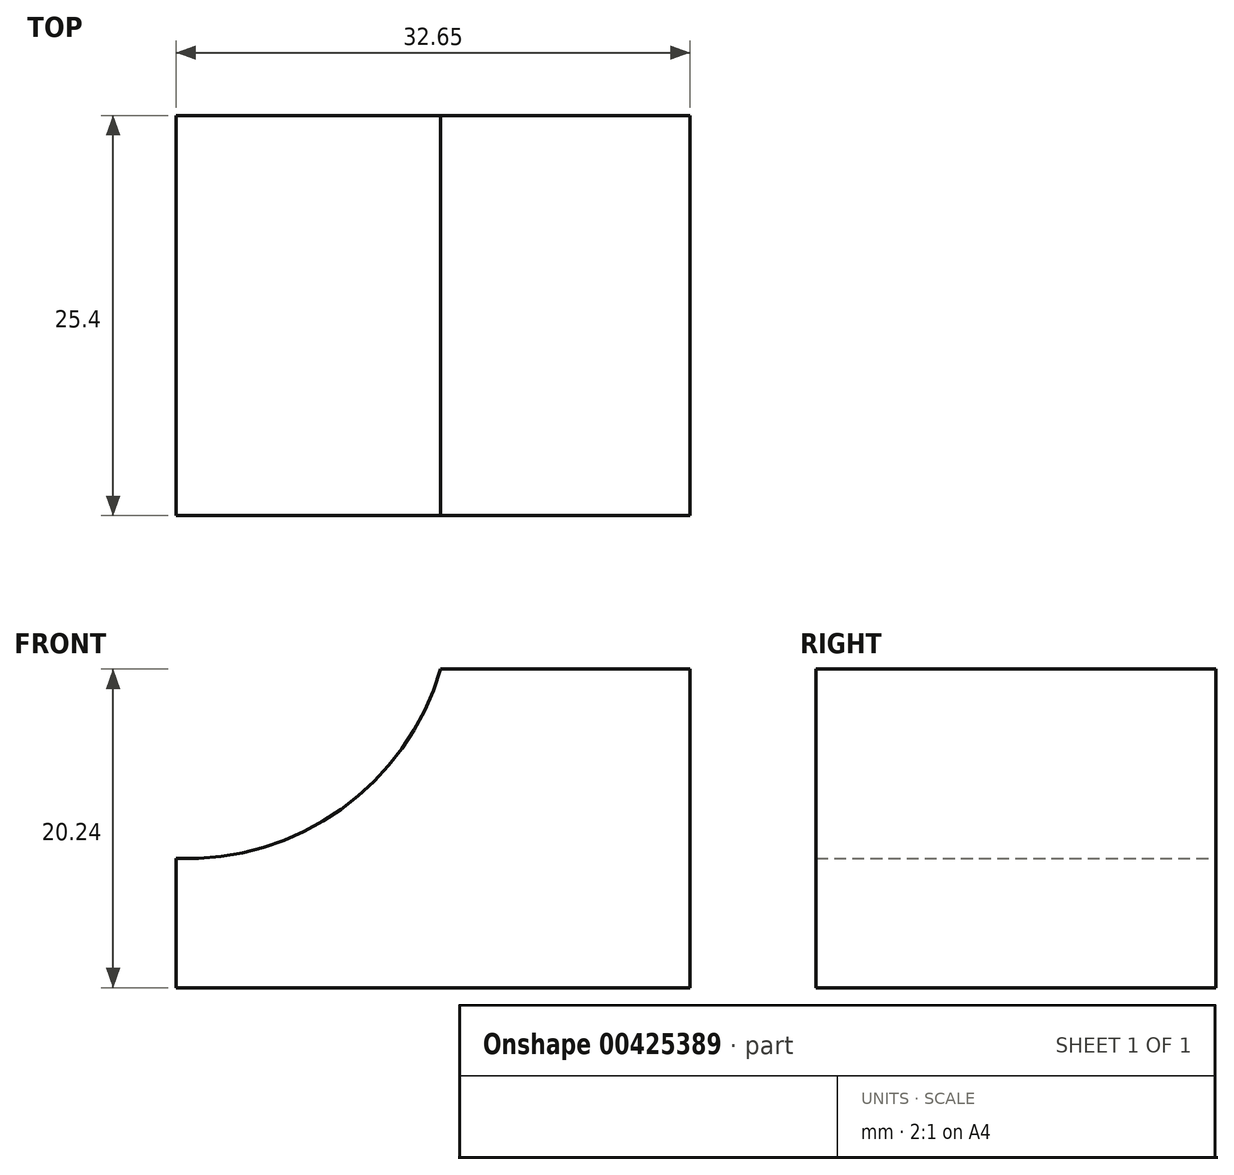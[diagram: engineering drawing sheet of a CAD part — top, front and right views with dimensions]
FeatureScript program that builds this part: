
annotation { "Feature Type Name" : "Feature", "Feature Type Description" : "" }
export const myFeature = defineFeature(function(context is Context, id is Id, definition is map)
    precondition{}
    {
        {
            var Q0;
            Q0=qCreatedBy(makeId("Front.planeOp"),FACE);
            var sketch = newSketch(context, id + "F0", { "sketchPlane" : qUnion([Q0])});
            skLineSegment(sketch, "E0", {"start": v(0, 20.62) * mm, "end": v(0, 0) * mm});
            skLineSegment(sketch, "E1", {"start": v(0, 0) * mm, "end": v(-32.65, 0) * mm});
            skLineSegment(sketch, "E2", {"start": v(-32.65, 0) * mm, "end": v(-32.65, 8.21) * mm});
            skArc(sketch, "E3", {"start": v(-32.65, 8.21) * mm, "mid": v(-22.18, 11.33) * mm, "end": v(-15.85, 20.24) * mm});
            skLineSegment(sketch, "E4", {"start": v(-15.85, 20.24) * mm, "end": v(1.34, 20.24) * mm});
            skSolve(sketch);
        }
        {
            var Q0;
            {var subQ1=sQuery(id+"F0.wireOp",EDGE,"E1");Q0=makeQuery(id+"F0.imprint","IMPRINT",FACE,{"disambiguationData":[TD([[makeQuery(id+"F0.imprint","IMPRINT",EDGE,{"derivedFrom":subQ1}),-1.0]])]});}
            extrude(context, id + "F1", {"entities" : qUnion([Q0]), "depth" : 25.4 * mm});
        }
    });
